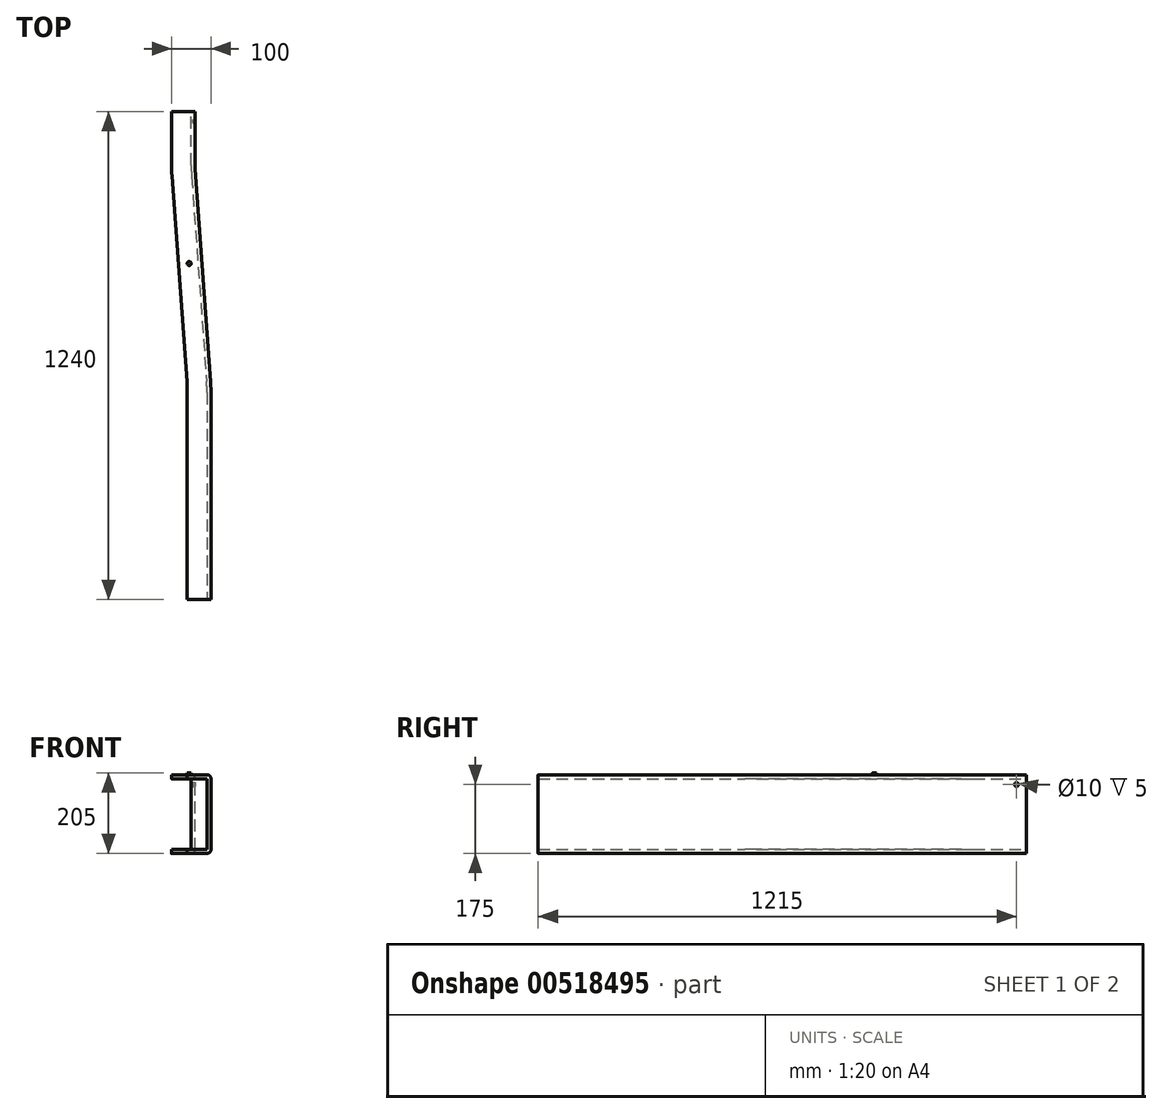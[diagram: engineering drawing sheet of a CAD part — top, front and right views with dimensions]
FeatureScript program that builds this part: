
annotation { "Feature Type Name" : "Feature", "Feature Type Description" : "" }
export const myFeature = defineFeature(function(context is Context, id is Id, definition is map)
    precondition{}
    {
        {
            var Q0;
            Q0=qCreatedBy(makeId("Top.planeOp"),FACE);
            var sketch = newSketch(context, id + "F0", { "sketchPlane" : qUnion([Q0])});
            skLineSegment(sketch, "E0", {"start": v(0, 0) * mm, "end": v(0, -150) * mm});
            skLineSegment(sketch, "E1", {"start": v(0, -150) * mm, "end": v(-40, -700) * mm});
            skLineSegment(sketch, "E2", {"start": v(-40, -700) * mm, "end": v(-40, -1240) * mm});
            skLineSegment(sketch, "E3", {"start": v(-40, -1240) * mm, "end": v(20, -1240) * mm});
            skLineSegment(sketch, "E4", {"start": v(20, -1240) * mm, "end": v(20, -700) * mm});
            skLineSegment(sketch, "E5", {"start": v(20, -700) * mm, "end": v(60, -150) * mm});
            skLineSegment(sketch, "E6", {"start": v(60, -150) * mm, "end": v(60, 0) * mm});
            skLineSegment(sketch, "E7", {"start": v(60, 0) * mm, "end": v(0, 0) * mm});
            skSolve(sketch);
        }
        {
            var Q0;
            Q0=qSketchRegion(id+"F0",true);
            extrude(context, id + "F1", {"entities" : qUnion([Q0]), "oppositeDirection" : true, "depth" : 200 * mm, "offsetDistance" : 25 * mm});
        }
        {
            var Q0;
            Q0=makeQuery(id+"F1.opExtrude","SWEPT_EDGE",EDGE,{"disambiguationData":[OSD([sQuery(id+"F0.wireOp",EDGE,"E1"),sQuery(id+"F0.wireOp",EDGE,"E2")])]});
            var Q1;
            Q1=makeQuery(id+"F1.opExtrude","SWEPT_EDGE",EDGE,{"disambiguationData":[OSD([sQuery(id+"F0.wireOp",EDGE,"E0"),sQuery(id+"F0.wireOp",EDGE,"E1")])]});
            var Q2;
            Q2=makeQuery(id+"F1.opExtrude","SWEPT_EDGE",EDGE,{"disambiguationData":[OSD([sQuery(id+"F0.wireOp",EDGE,"E4"),sQuery(id+"F0.wireOp",EDGE,"E5")])]});
            var Q3;
            Q3=makeQuery(id+"F1.opExtrude","SWEPT_EDGE",EDGE,{"disambiguationData":[OSD([sQuery(id+"F0.wireOp",EDGE,"E5"),sQuery(id+"F0.wireOp",EDGE,"E6")])]});
            fillet(context, id + "F2", {"entities" : qUnion([Q0, Q1, Q2, Q3]), "radius" : 400 * mm, "tangentPropagation" : true, "allowEdgeOverflow" : false});
        }
        {
            var Q0;
            Q0=makeQuery(id+"F1.opExtrude","CAP_EDGE",EDGE,{"disambiguationData":[OSD([sQuery(id+"F0.wireOp",EDGE,"E1")])],"isStart":true});
            var Q1;
            Q1=makeQuery(id+"F1.opExtrude","CAP_EDGE",EDGE,{"disambiguationData":[OSD([sQuery(id+"F0.wireOp",EDGE,"E1")])],"isStart":false});
            fillet(context, id + "F3", {"entities" : qUnion([Q0, Q1]), "radius" : 10 * mm, "tangentPropagation" : true, "allowEdgeOverflow" : false});
        }
        {
            var Q0;
            Q0=makeQuery(id+"F1.opExtrude","SWEPT_FACE",FACE,{"disambiguationData":[OSD([sQuery(id+"F0.wireOp",EDGE,"E4")])]});
            var Q1;
            Q1=makeQuery(id+"F2.opFillet","BLEND_FACE",FACE,{"disambiguationData":[OSD([sQuery(id+"F0.wireOp",EDGE,"E4"),sQuery(id+"F0.wireOp",EDGE,"E5")])]});
            var Q2;
            Q2=makeQuery(id+"F1.opExtrude","SWEPT_FACE",FACE,{"disambiguationData":[OSD([sQuery(id+"F0.wireOp",EDGE,"E5")])]});
            var Q3;
            Q3=makeQuery(id+"F2.opFillet","BLEND_FACE",FACE,{"disambiguationData":[OSD([sQuery(id+"F0.wireOp",EDGE,"E5"),sQuery(id+"F0.wireOp",EDGE,"E6")])]});
            var Q4;
            Q4=makeQuery(id+"F1.opExtrude","SWEPT_FACE",FACE,{"disambiguationData":[OSD([sQuery(id+"F0.wireOp",EDGE,"E6")])]});
            var Q5;
            Q5=makeQuery(id+"F1.opExtrude","SWEPT_FACE",FACE,{"disambiguationData":[OSD([sQuery(id+"F0.wireOp",EDGE,"E7")])]});
            var Q6;
            Q6=makeQuery(id+"F1.opExtrude","SWEPT_FACE",FACE,{"disambiguationData":[OSD([sQuery(id+"F0.wireOp",EDGE,"E3")])]});
            shell(context, id + "F4", {"entities" : qUnion([Q0, Q1, Q2, Q3, Q4, Q5, Q6]), "thickness" : 10 * mm});
        }
        {
            var Q0;
            Q0=makeQuery(id+"F1.opExtrude","SWEPT_FACE",FACE,{"disambiguationData":[OSD([sQuery(id+"F0.wireOp",EDGE,"E0")])]});
            var sketch = newSketch(context, id + "F5", { "sketchPlane" : qUnion([Q0])});
            skCircle(sketch, "E8", {"center": v(25, -25) * mm, "radius": 5 * mm});
            skSolve(sketch);
        }
        {
            var Q0;
            Q0=qSketchRegion(id+"F5",true);
            extrude(context, id + "F6", {"entities" : qUnion([Q0]), "operationType" : NewBodyOperationType.REMOVE, "oppositeDirection" : true, "depth" : 5 * mm, "offsetDistance" : 25 * mm});
        }
        {
            var Q0;
            Q0=makeQuery(id+"F1.opExtrude","SWEPT_BODY",BODY,{"disambiguationData":[OSD([sQuery(id+"F0.wireOp",EDGE,"E0"),sQuery(id+"F0.wireOp",EDGE,"E1"),sQuery(id+"F0.wireOp",EDGE,"E2"),sQuery(id+"F0.wireOp",EDGE,"E3"),sQuery(id+"F0.wireOp",EDGE,"E4"),sQuery(id+"F0.wireOp",EDGE,"E5"),sQuery(id+"F0.wireOp",EDGE,"E6"),sQuery(id+"F0.wireOp",EDGE,"E7")])]});
            var Q1;
            Q1=qCreatedBy(makeId("Right.planeOp"),FACE);
            mirror(context, id + "F7", {"entities" : qUnion([Q0]), "mirrorPlane" : qUnion([Q1])});
        }
        {
            var Q0;
            Q0=makeQuery(id+"F1.opExtrude","SWEPT_BODY",BODY,{"disambiguationData":[OSD([sQuery(id+"F0.wireOp",EDGE,"E0"),sQuery(id+"F0.wireOp",EDGE,"E1"),sQuery(id+"F0.wireOp",EDGE,"E2"),sQuery(id+"F0.wireOp",EDGE,"E3"),sQuery(id+"F0.wireOp",EDGE,"E4"),sQuery(id+"F0.wireOp",EDGE,"E5"),sQuery(id+"F0.wireOp",EDGE,"E6"),sQuery(id+"F0.wireOp",EDGE,"E7")])]});
            deleteBodies(context, id + "F8", {"entities" : qUnion([Q0])});
        }
        {
            var Q0;
            Q0=makeQuery(id+"F7.opPattern","COPY",FACE,{"derivedFrom":makeQuery(id+"F1.opExtrude","CAP_FACE",FACE,{"disambiguationData":[OSD([sQuery(id+"F0.wireOp",EDGE,"E0"),sQuery(id+"F0.wireOp",EDGE,"E1"),sQuery(id+"F0.wireOp",EDGE,"E2"),sQuery(id+"F0.wireOp",EDGE,"E3"),sQuery(id+"F0.wireOp",EDGE,"E4"),sQuery(id+"F0.wireOp",EDGE,"E5"),sQuery(id+"F0.wireOp",EDGE,"E6"),sQuery(id+"F0.wireOp",EDGE,"E7")])],"isStart":true}),"instanceName":"1"});
            var sketch = newSketch(context, id + "F9", { "sketchPlane" : qUnion([Q0])});
            skCircle(sketch, "E9", {"center": v(-15, -386) * mm, "radius": 5 * mm});
            skSolve(sketch);
        }
        {
            var Q0;
            Q0 = qSketchRegion(id + "F9", true);
            extrude(context, id + "F10", {"entities" : qUnion([Q0]), "operationType" : NewBodyOperationType.ADD, "depth" : 5 * mm, "offsetDistance" : 25 * mm});
        }
    });
